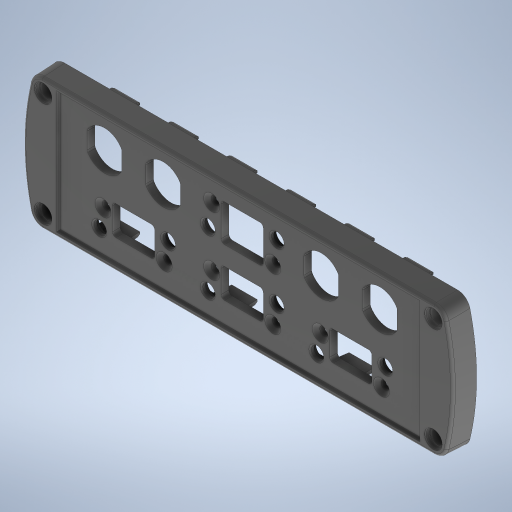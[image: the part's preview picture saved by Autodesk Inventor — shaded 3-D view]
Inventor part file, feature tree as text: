
AUTODESK INVENTOR PART (.ipt)
format: ipt  version: 2024 (Build 280153000, 153)  size: 1,383,936 bytes
history: native  units: mm
features: extrude x8, sketch x7, fillet x4, chamfer x4, plane x2, mirror x1, hole x1, other x1
ambient origin geometry x8: Origin, YZ Plane, XZ Plane, XY Plane, X Axis, Y Axis, Z Axis, Center Point
bodies: Solid1 (feature_tree)
feature tree (28):
  extrude  "Extrusion1"  TaperAngle=0.0deg  [1 undecoded]
  fillet  "Fillet1"  Radius=6.9mm
  plane  "Work Plane1"
  extrude  "Extrusion4"  [1 undecoded]
  fillet  "Fillet6"  Radius=15.4mm
  chamfer  "Chamfer2"  [1 undecoded]
  mirror  "Mirror1"
  plane  "Work Plane2"
  extrude  "Extrusion7"  Depth=0.2mm TaperAngle=45.0deg
  extrude  "Extrusion11"  Depth=1.5mm
  extrude  "Extrusion12"  Depth=1.5mm
  fillet  "Fillet4"  Radius=10.075mm
  chamfer  "Chamfer4"  Distance=42.584mm
  extrude  "Extrusion13"  Depth=1.5mm
  extrude  "Extrusion14"  Depth=10.0mm TaperAngle=0.0deg
  fillet  "Fillet5"  Radius=0.5mm
  extrude  "Extrusion15"  Depth=1.5mm
  chamfer  "Chamfer5"  Distance=10.075mm
  hole  "Hole1"  [1 undecoded]
  chamfer  "Chamfer3"  Distance=6.9mm
  sketch  "Sketch20"  dims[d3=9.0mm d15=0.0mm d16=0.0mm d21=6.9mm]
  sketch  "Sketch21"  dims[d23=1.35mm d26=-1.5mm d40=15.4mm]
  sketch  "Sketch24"  dims[d43=15.4mm]
  sketch  "Sketch25"  dims[d44=0.0mm]
  sketch  "Sketch27"  dims[d45=31.0mm d46=0.0mm d47=0.0mm d48=0.2mm d49=2.0mm d50=45.0deg d65=4.85mm d66=4.85mm d67=27.0mm d68=9.0mm d69=3.3mm d70=3.3mm d71=24.0mm d72=16.55mm d73=11.55mm d74=6.35mm d75=1.85mm d76=5.225mm d77=6.9mm d78=10.075mm d79=10.075mm d80=42.584mm d82=7.0mm d83=10.0mm d84=0.0mm d85=0.5mm d86=2.0mm d87=45.0deg d101=10.075mm d102=4.85mm d103=4.85mm d104=27.0mm d105=9.0mm d106=3.3mm d107=3.3mm d108=24.0mm d109=16.55mm d110=11.55mm d111=6.35mm d112=1.85mm d113=5.225mm d114=10.075mm d115=12.0mm d116=6.9mm d117=42.584mm d118=7.0mm d119=7.0mm d122=12.0mm d127=3.25mm d128=6.0mm d129=6.25mm d130=2.0mm d131=90.0deg d132=8.0mm d133=20.594885mm d136=10.0mm d137=0.0mm d138=0.2mm d139=0.0mm d140=3.0mm d141=0.2mm d142=2.0mm d143=45.0deg d144=0.2mm d145=2.0mm d146=45.0deg d147=10.0mm d148=0.0mm d149=8.0mm d150=12.5mm d151=8.0mm d152=12.5mm d153=12.5mm d154=8.0mm d155=8.0mm d156=12.5mm d157=4.5mm d160=4.5mm d161=1.0mm d164=1.0mm d167=28.699852mm d169=20.0mm d171=42.584mm d172=10.0mm d174=10.0mm d176=7.0mm d177=7.0mm d178=7.0mm d179=1.0mm d180=4.5mm d181=7.001437mm d182=16.55mm d183=14.55mm d184=3.3mm d185=4.85mm d186=4.85mm d187=3.3mm d188=5.225mm d189=9.0mm d190=4.5mm d191=27.0mm d192=24.0mm d193=3.725mm d194=9.0mm d195=4.5mm d197=9.125mm d198=10.0mm d199=0.0mm d200=1.35mm d201=7.0mm d202=7.0mm d203=1.9mm d204=0.0mm d205=0.0mm d206=8.871486mm d207=3.839257mm d208=16.55mm d209=13.6mm d210=6.8mm d211=13.6mm d212=6.8mm d213=1.5mm d214=16.95mm d215=11.95mm d216=5.975mm d217=8.475mm d218=8.475mm d219=5.975mm d220=8.475mm d221=5.975mm d222=16.95mm d223=14.95mm d224=8.475mm d225=7.475mm d226=3.0mm d227=3.0mm d228=3.0mm d229=3.0mm d230=3.0mm d231=3.0mm d232=3.0mm d233=3.0mm d234=3.0mm d235=3.0mm d236=3.0mm d237=3.0mm d239=3.0mm d240=3.0mm d241=3.0mm d242=3.0mm d243=3.0mm d244=3.0mm d245=3.0mm d246=3.0mm d247=3.0mm d248=3.0mm d249=3.0mm d250=3.0mm d251=8.0mm d252=8.0mm d253=3.0mm d254=3.0mm]
  sketch  "Sketch22"  dims[d41=11.5mm]
  sketch  "Sketch23"  dims[d42=54.0mm]
  other  "1009799_3D"
note: 4 required parameter values undecoded (feature->parameter linkage not recoverable at this tier; creation-order binding heuristic only, values carry confidence <= 0.55)
